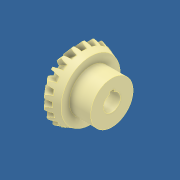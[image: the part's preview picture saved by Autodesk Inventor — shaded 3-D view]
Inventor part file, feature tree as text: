
AUTODESK INVENTOR PART (.ipt)
format: ipt  version: 2018 (Build 220112000, 112)  size: 336,384 bytes
history: native  units: mm
features: extrude x1, sketch x1, pattern_circular x1
ambient origin geometry x8: Origin, YZ Plane, XZ Plane, XY Plane, X Axis, Y Axis, Z Axis, Center Point
bodies: Solid1 (feature_tree)
feature tree (3):
  extrude  "Extrusion3"  Depth=1.0mm
  sketch  "Sketch3"  dims[d12=2.0mm d13=1.0mm d14=1.0mm d15=0.0mm d16=0.0mm]
  pattern_circular  "CirPattern1"
